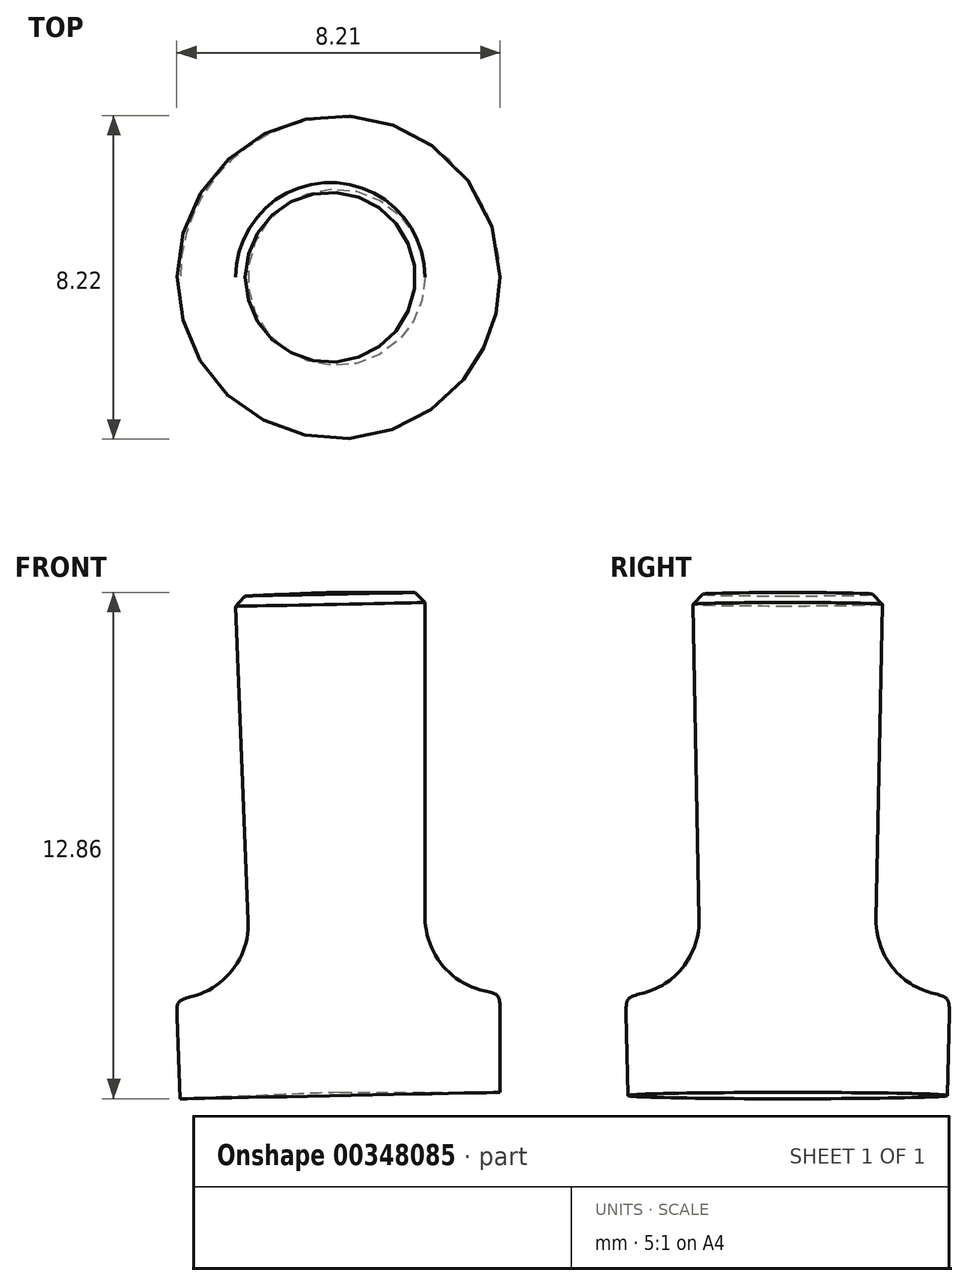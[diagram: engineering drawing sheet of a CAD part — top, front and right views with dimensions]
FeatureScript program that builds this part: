
annotation { "Feature Type Name" : "Feature", "Feature Type Description" : "" }
export const myFeature = defineFeature(function(context is Context, id is Id, definition is map)
    precondition{}
    {
        {
            var Q0;
            Q0=qCreatedBy(makeId("Front.planeOp"),FACE);
            var sketch = newSketch(context, id + "F0", { "sketchPlane" : qUnion([Q0])});
            skLineSegment(sketch, "E0.top", {"start": v(-0.25, 12.7) * mm, "end": v(2.16, 12.7) * mm});
            skLineSegment(sketch, "E0.right", {"start": v(2.16, 4.45) * mm, "end": v(2.16, 12.7) * mm});
            skLineSegment(sketch, "E1.top", {"start": v(4.06, 2.54) * mm, "end": v(4.06, 2.54) * mm});
            skArc(sketch, "E2.filletArc", {"start": v(2.16, 4.45) * mm, "mid": v(2.72, 3.1) * mm, "end": v(4.06, 2.54) * mm});
            skPoint(sketch, "E0.bottom.start.orphan", {"position": v(0, 0) * mm});
            skLineSegment(sketch, "E3", {"start": v(0, 0) * mm, "end": v(4.06, 0) * mm});
            skLineSegment(sketch, "E4", {"start": v(4.06, 2.54) * mm, "end": v(4.06, 0) * mm});
            skLineSegment(sketch, "E5", {"start": v(-0.25, 12.7) * mm, "end": v(0, 0) * mm});
            skSolve(sketch);
        }
        {
            var Q0;
            Q0=makeQuery(id+"F0.imprint","IMPRINT",FACE,{"disambiguationData":[TD([[makeQuery(id+"F0.imprint","IMPRINT",EDGE,{"derivedFrom":sQuery(id+"F0.wireOp",EDGE,"E0.top")}),-1.0]])]});
            var Q1;
            Q1=sQuery(id+"F0.wireOp",EDGE,"E0.top");
            var Q2;
            Q2=sQuery(id+"F0.wireOp",EDGE,"E0.right");
            var Q3;
            Q3=sQuery(id+"F0.wireOp",EDGE,"E2.filletArc");
            var Q4;
            Q4=sQuery(id+"F0.wireOp",EDGE,"E4");
            var Q5;
            Q5=sQuery(id+"F0.wireOp",EDGE,"E3");
            var Q6;
            Q6=sQuery(id+"F0.wireOp",EDGE,"E5");
            revolve(context, id + "F1", {"entities" : qUnion([Q0]), "surfaceEntities" : qUnion([Q1, Q2, Q3, Q4, Q5]), "axis" : qUnion([Q6]), "revolveType" : RevolveType.FULL});
        }
        {
            var Q0;
            Q0=makeQuery(id+"F1.opRevolve","SWEPT_EDGE",EDGE,{"disambiguationData":[OSD([sQuery(id+"F0.wireOp",VERTEX,"E0.right.end")])]});
            var Q1;
            Q1=makeQuery(id+"F1.opRevolve","SWEPT_EDGE",EDGE,{"disambiguationData":[OSD([sQuery(id+"F0.wireOp",EDGE,"E0.top"),sQuery(id+"F0.wireOp",EDGE,"E0.right")])]});
            chamfer(context, id + "F2", {"entities" : qUnion([Q0, Q1]), "width" : 0.25 * mm, "tangentPropagation" : true});
        }
        {
            var Q0;
            Q0=makeQuery(id+"F1.opRevolve","SWEPT_EDGE",EDGE,{"disambiguationData":[OSD([sQuery(id+"F0.wireOp",EDGE,"E2.filletArc"),sQuery(id+"F0.wireOp",EDGE,"E4")])]});
            fillet(context, id + "F3", {"entities" : qUnion([Q0]), "radius" : 0.5 * mm, "tangentPropagation" : true, "rho" : 0.7, "crossSection" : FilletCrossSection.CONIC, "allowEdgeOverflow" : false});
        }
    });
